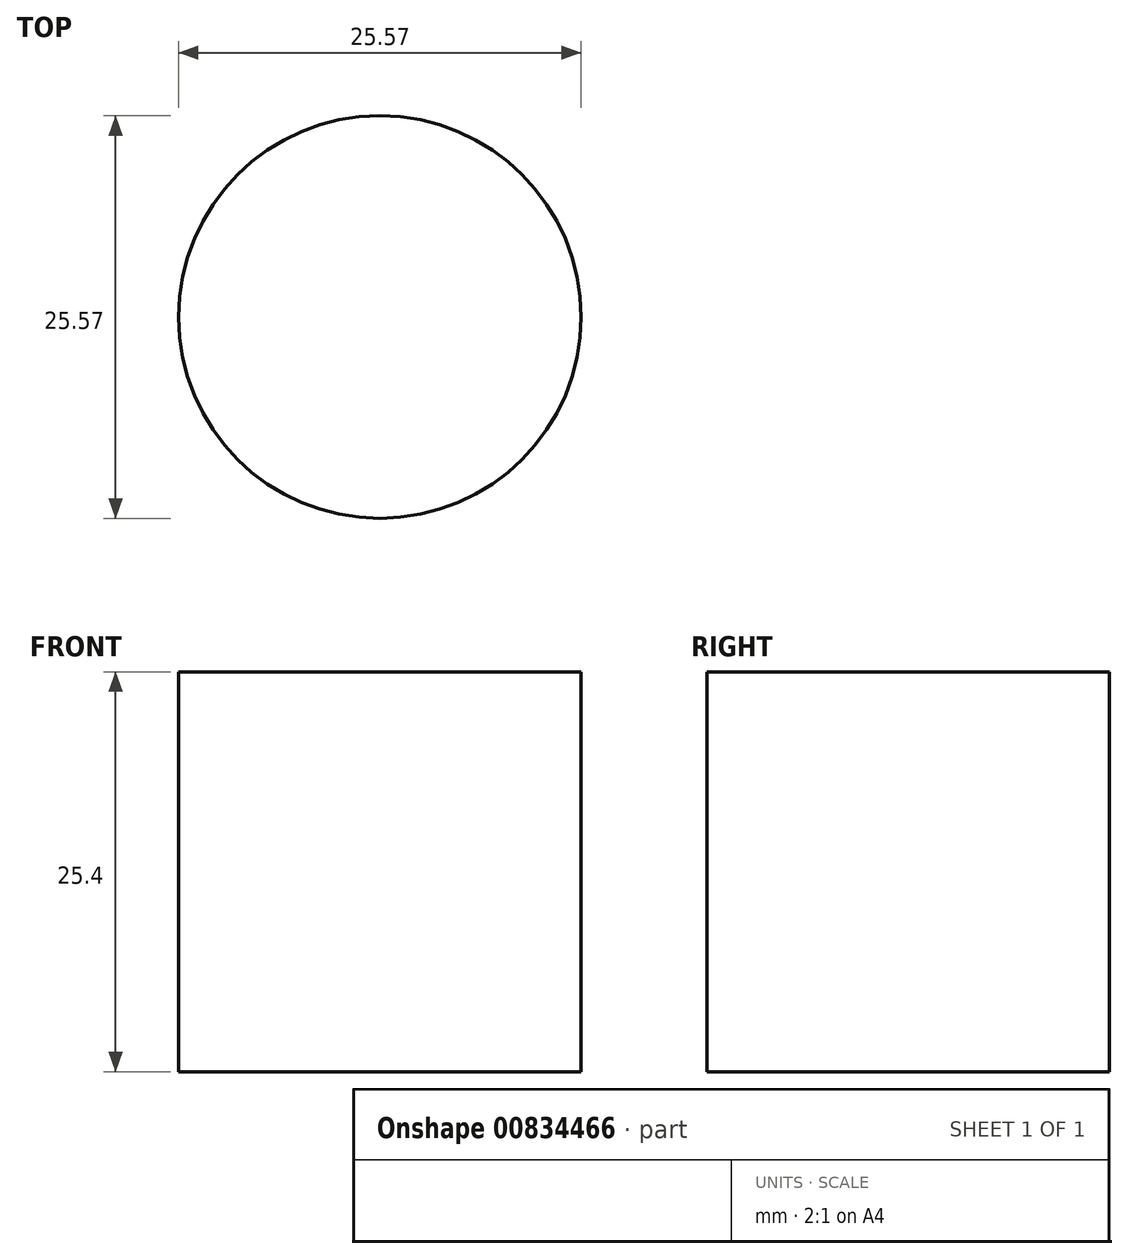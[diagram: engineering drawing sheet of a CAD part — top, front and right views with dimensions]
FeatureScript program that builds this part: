
annotation { "Feature Type Name" : "Feature", "Feature Type Description" : "" }
export const myFeature = defineFeature(function(context is Context, id is Id, definition is map)
    precondition{}
    {
        {
            var Q0;
            Q0=qCreatedBy(makeId("Top.planeOp"),FACE);
            var sketch = newSketch(context, id + "F0", { "sketchPlane" : qUnion([Q0])});
            skLineSegment(sketch, "E0.bottom", {"start": v(33.24, 55.44) * mm, "end": v(-36.22, 55.44) * mm});
            skLineSegment(sketch, "E0.top", {"start": v(33.24, -50.7) * mm, "end": v(-36.22, -50.7) * mm});
            skLineSegment(sketch, "E0.left", {"start": v(33.24, 55.44) * mm, "end": v(33.24, -50.7) * mm});
            skLineSegment(sketch, "E0.right", {"start": v(-36.22, 55.44) * mm, "end": v(-36.22, -50.7) * mm});
            skSolve(sketch);
        }
        {
            var Q0;
            Q0=makeQuery(id+"F0.imprint","IMPRINT",FACE,{"disambiguationData":[TD([[makeQuery(id+"F0.imprint","IMPRINT",EDGE,{"derivedFrom":sQuery(id+"F0.wireOp",EDGE,"E0.bottom")}),1.0]])]});
            extrude(context, id + "F1", {"entities" : qUnion([Q0]), "depth" : 25.4 * mm, "offsetDistance" : 25.4 * mm});
        }
        {
            var Q0;
            Q0=makeQuery(id+"F1.opExtrude","CAP_EDGE",EDGE,{"disambiguationData":[OSD([sQuery(id+"F0.wireOp",EDGE,"E0.left")])],"isStart":false});
            var Q1;
            Q1=makeQuery(id+"F1.opExtrude","CAP_EDGE",EDGE,{"disambiguationData":[OSD([sQuery(id+"F0.wireOp",EDGE,"E0.top")])],"isStart":false});
            var Q2;
            Q2=makeQuery(id+"F1.opExtrude","CAP_EDGE",EDGE,{"disambiguationData":[OSD([sQuery(id+"F0.wireOp",EDGE,"E0.right")])],"isStart":false});
            var Q3;
            Q3=makeQuery(id+"F1.opExtrude","CAP_EDGE",EDGE,{"disambiguationData":[OSD([sQuery(id+"F0.wireOp",EDGE,"E0.bottom")])],"isStart":false});
            var Q4;
            Q4=makeQuery(id+"F1.opExtrude","SWEPT_EDGE",EDGE,{"disambiguationData":[OSD([sQuery(id+"F0.wireOp",EDGE,"E0.top"),sQuery(id+"F0.wireOp",EDGE,"E0.left")])]});
            var Q5;
            Q5=makeQuery(id+"F1.opExtrude","SWEPT_EDGE",EDGE,{"disambiguationData":[OSD([sQuery(id+"F0.wireOp",EDGE,"E0.bottom"),sQuery(id+"F0.wireOp",EDGE,"E0.left")])]});
            var Q6;
            Q6=makeQuery(id+"F1.opExtrude","SWEPT_EDGE",EDGE,{"disambiguationData":[OSD([sQuery(id+"F0.wireOp",EDGE,"E0.top"),sQuery(id+"F0.wireOp",EDGE,"E0.right")])]});
            var Q7;
            Q7=makeQuery(id+"F1.opExtrude","SWEPT_EDGE",EDGE,{"disambiguationData":[OSD([sQuery(id+"F0.wireOp",EDGE,"E0.bottom"),sQuery(id+"F0.wireOp",EDGE,"E0.right")])]});
            fillet(context, id + "F2", {"entities" : qUnion([Q0, Q1, Q2, Q3, Q4, Q5, Q6, Q7]), "radius" : 5.08 * mm, "tangentPropagation" : true, "allowEdgeOverflow" : false});
        }
        {
            var Q0;
            Q0=makeQuery(id+"F1.opExtrude","CAP_FACE",FACE,{"disambiguationData":[OSD([sQuery(id+"F0.wireOp",EDGE,"E0.bottom"),sQuery(id+"F0.wireOp",EDGE,"E0.top"),sQuery(id+"F0.wireOp",EDGE,"E0.left"),sQuery(id+"F0.wireOp",EDGE,"E0.right")])],"isStart":false});
            var sketch = newSketch(context, id + "F3", { "sketchPlane" : qUnion([Q0])});
            skCircle(sketch, "E1", {"center": v(-4.7, -7.83) * mm, "radius": 12.78 * mm});
            skSolve(sketch);
        }
        {
            var Q0;
            Q0=makeQuery(id+"F3.imprint","IMPRINT",FACE,{"disambiguationData":[TD([[makeQuery(id+"F3.imprint","IMPRINT",EDGE,{"derivedFrom":sQuery(id+"F3.wireOp",EDGE,"E1")}),1.0]])]});
            extrude(context, id + "F4", {"entities" : qUnion([Q0]), "operationType" : NewBodyOperationType.INTERSECT, "oppositeDirection" : true, "depth" : 25.4 * mm, "offsetDistance" : 25.4 * mm});
        }
    });
